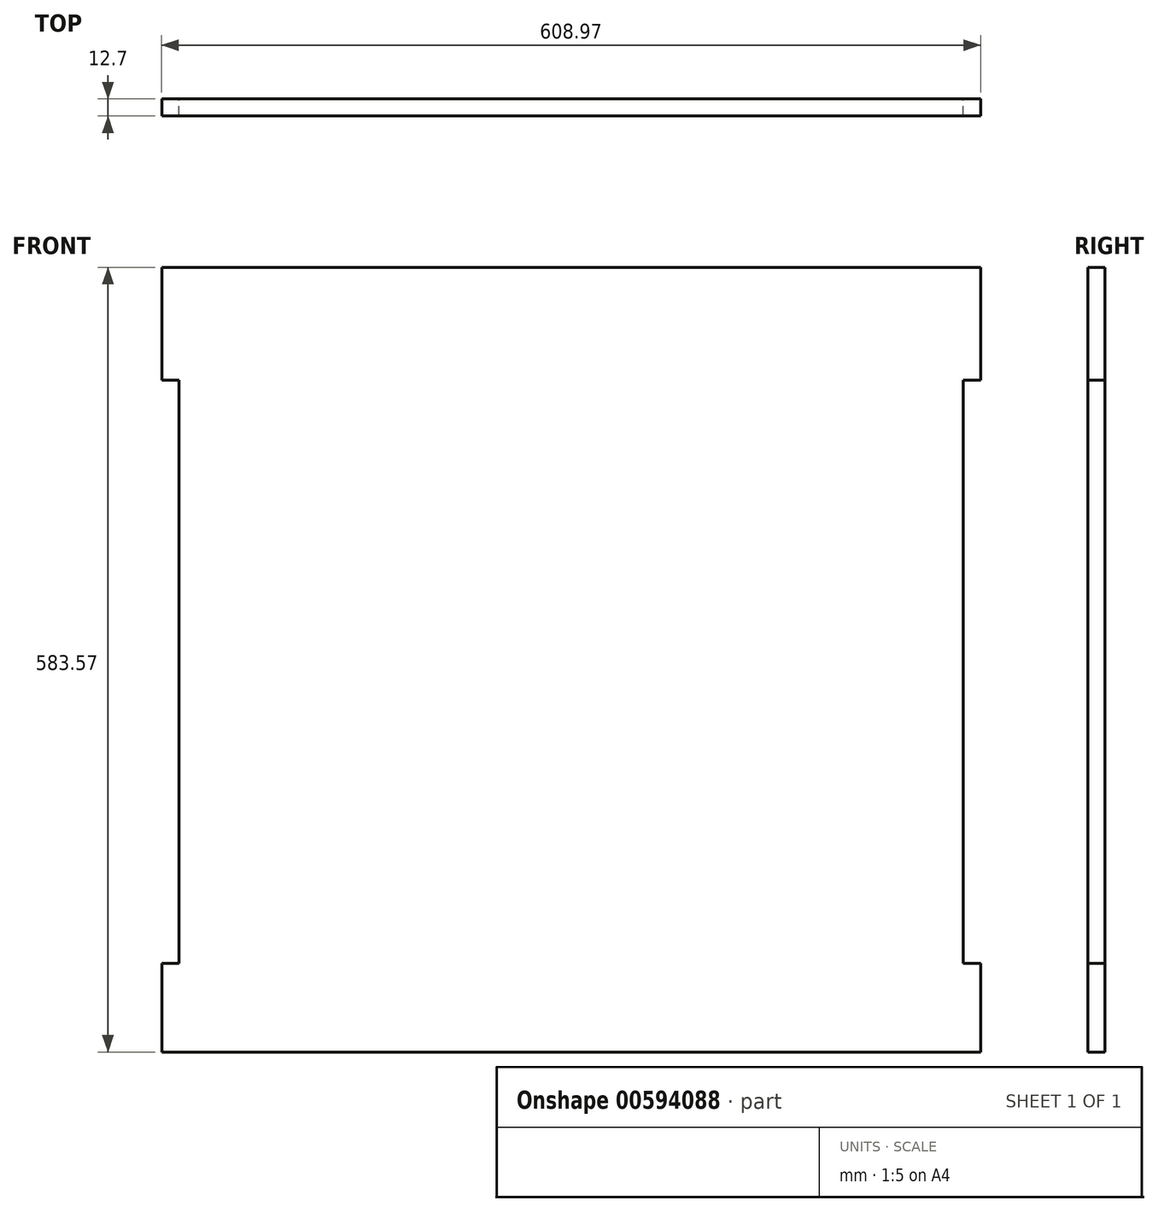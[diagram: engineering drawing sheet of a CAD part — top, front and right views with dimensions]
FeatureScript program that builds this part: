
annotation { "Feature Type Name" : "Feature", "Feature Type Description" : "" }
export const myFeature = defineFeature(function(context is Context, id is Id, definition is map)
    precondition{}
    {
        {
            var Q0;
            Q0=qCreatedBy(makeId("Front.planeOp"),FACE);
            var sketch = newSketch(context, id + "F0", { "sketchPlane" : qUnion([Q0])});
            skLineSegment(sketch, "E0.bottom", {"start": v(0, 0) * mm, "end": v(-583.57, 0) * mm});
            skLineSegment(sketch, "E0.top", {"start": v(0, 583.57) * mm, "end": v(-583.57, 583.57) * mm});
            skLineSegment(sketch, "E0.left", {"start": v(0, 0) * mm, "end": v(0, 583.57) * mm});
            skLineSegment(sketch, "E0.right", {"start": v(-583.57, 0) * mm, "end": v(-583.57, 583.57) * mm});
            skLineSegment(sketch, "E1", {"start": v(0, 583.57) * mm, "end": v(12.7, 583.57) * mm});
            skLineSegment(sketch, "E2", {"start": v(12.7, 583.57) * mm, "end": v(12.7, 499.75) * mm});
            skLineSegment(sketch, "E3", {"start": v(12.7, 499.75) * mm, "end": v(0, 499.75) * mm});
            skLineSegment(sketch, "E4", {"start": v(0, 66.04) * mm, "end": v(12.7, 66.04) * mm});
            skLineSegment(sketch, "E5", {"start": v(12.7, 66.04) * mm, "end": v(12.7, 0) * mm});
            skLineSegment(sketch, "E6", {"start": v(12.7, 0) * mm, "end": v(0, 0) * mm});
            skLineSegment(sketch, "E7", {"start": v(-583.57, 66.04) * mm, "end": v(-596.27, 66.04) * mm});
            skLineSegment(sketch, "E8", {"start": v(-596.27, 66.04) * mm, "end": v(-596.27, 0) * mm});
            skLineSegment(sketch, "E9", {"start": v(-596.27, 0) * mm, "end": v(-583.57, 0) * mm});
            skLineSegment(sketch, "E10", {"start": v(-583.57, 499.75) * mm, "end": v(-596.27, 499.75) * mm});
            skLineSegment(sketch, "E11", {"start": v(-596.27, 499.75) * mm, "end": v(-596.27, 583.57) * mm});
            skLineSegment(sketch, "E12", {"start": v(-596.27, 583.56) * mm, "end": v(-583.57, 583.56) * mm});
            skLineSegment(sketch, "E13", {"start": v(0, 583.57) * mm, "end": v(0, 499.75) * mm});
            skLineSegment(sketch, "E14", {"start": v(0, 66.04) * mm, "end": v(0, 0) * mm});
            skLineSegment(sketch, "E15", {"start": v(-583.57, 0) * mm, "end": v(-583.57, 66.04) * mm});
            skLineSegment(sketch, "E16", {"start": v(-583.57, 499.75) * mm, "end": v(-583.57, 583.57) * mm});
            skSolve(sketch);
        }
        {
            var Q0;
            Q0=makeQuery(id+"F0.imprint","IMPRINT",FACE,{"disambiguationData":[TD([[makeQuery(id+"F0.imprint","IMPRINT",EDGE,{"derivedFrom":sQuery(id+"F0.wireOp",EDGE,"E10")}),-1.0]])]});
            var Q1;
            Q1=makeQuery(id+"F0.imprint","IMPRINT",FACE,{"disambiguationData":[TD([[makeQuery(id+"F0.imprint","IMPRINT",EDGE,{"derivedFrom":sQuery(id+"F0.wireOp",EDGE,"E0.bottom")}),-1.0]])]});
            var Q2;
            Q2=makeQuery(id+"F0.imprint","IMPRINT",FACE,{"disambiguationData":[TD([[makeQuery(id+"F0.imprint","IMPRINT",EDGE,{"derivedFrom":sQuery(id+"F0.wireOp",EDGE,"E7")}),1.0]])]});
            var Q3;
            Q3=makeQuery(id+"F0.imprint","IMPRINT",FACE,{"disambiguationData":[TD([[makeQuery(id+"F0.imprint","IMPRINT",EDGE,{"derivedFrom":sQuery(id+"F0.wireOp",EDGE,"E4")}),-1.0]])]});
            var Q4;
            Q4=makeQuery(id+"F0.imprint","IMPRINT",FACE,{"disambiguationData":[TD([[makeQuery(id+"F0.imprint","IMPRINT",EDGE,{"derivedFrom":sQuery(id+"F0.wireOp",EDGE,"E1")}),-1.0]])]});
            extrude(context, id + "F1", {"entities" : qUnion([Q0, Q1, Q2, Q3, Q4]), "depth" : 12.7 * mm, "offsetDistance" : 25.4 * mm});
        }
    });
